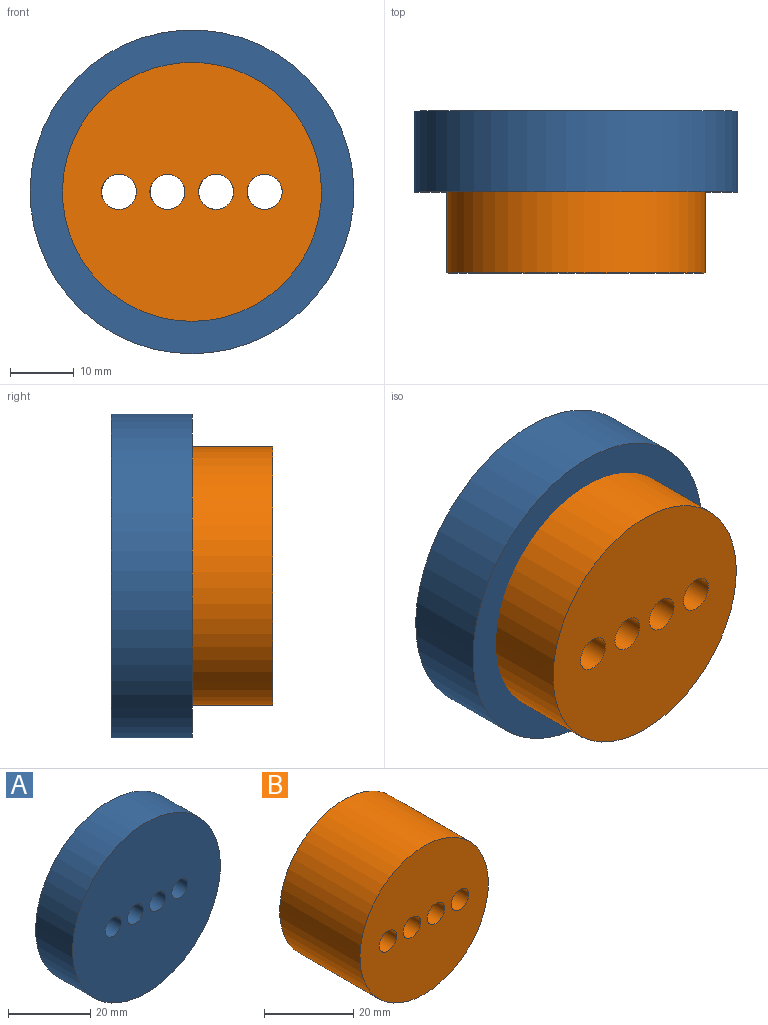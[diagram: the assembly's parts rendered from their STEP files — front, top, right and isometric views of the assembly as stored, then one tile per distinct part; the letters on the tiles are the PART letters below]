
ASSEMBLY  parts=2 mates=1
PART A: 7 faces, bbox 50.8x12.7x50.8 mm
  f0: cylinder r=25.4mm len=50.8mm, axis (0,1,0), area 2026.8mm2, adj f1,f2
  f1: plane 50.8x50.8mm, normal (0,-1,0), area 1931.8mm2, adj f0,f3,f4,f5,f6
  f2: plane 50.8x50.8mm, normal (0,1,0), area 1931.8mm2, adj f0,f3,f4,f5,f6
  f3: cylinder r=2.75mm len=12.7mm, axis (0,-1,0), area 219.4mm2, adj f1,f2
  f4: cylinder r=2.75mm len=12.7mm, axis (0,-1,0), area 219.4mm2, adj f1,f2
  f5: cylinder r=2.75mm len=12.7mm, axis (0,-1,0), area 219.4mm2, adj f1,f2
  f6: cylinder r=2.75mm len=12.7mm, axis (0,-1,0), area 219.4mm2, adj f1,f2
PART B: 7 faces, bbox 40.6x25.4x40.6 mm
  f0: cylinder r=20.32mm len=40.64mm, axis (0,1,0), area 3242.9mm2, adj f1,f2
  f1: plane 40.64x40.64mm, normal (0,-1,0), area 1202.1mm2, adj f0,f3,f4,f5,f6
  f2: plane 40.64x40.64mm, normal (0,1,0), area 1202.1mm2, adj f0,f3,f4,f5,f6
  f3: cylinder r=2.75mm len=25.4mm, axis (0,1,0), area 438.9mm2, adj f1,f2
  f4: cylinder r=2.75mm len=25.4mm, axis (0,1,0), area 438.9mm2, adj f1,f2
  f5: cylinder r=2.75mm len=25.4mm, axis (0,1,0), area 438.9mm2, adj f1,f2
  f6: cylinder r=2.75mm len=25.4mm, axis (0,1,0), area 438.9mm2, adj f1,f2
PLACE A rot(axis=(0,1,0),0deg) t=(-30.08,1,-94.26)mm
PLACE B t=(-30.08,1,-94.26)mm
MATE parallel B.f0 <-> A.f0  axis (0,1,0) through (-30.07,1,-94.26)mm
